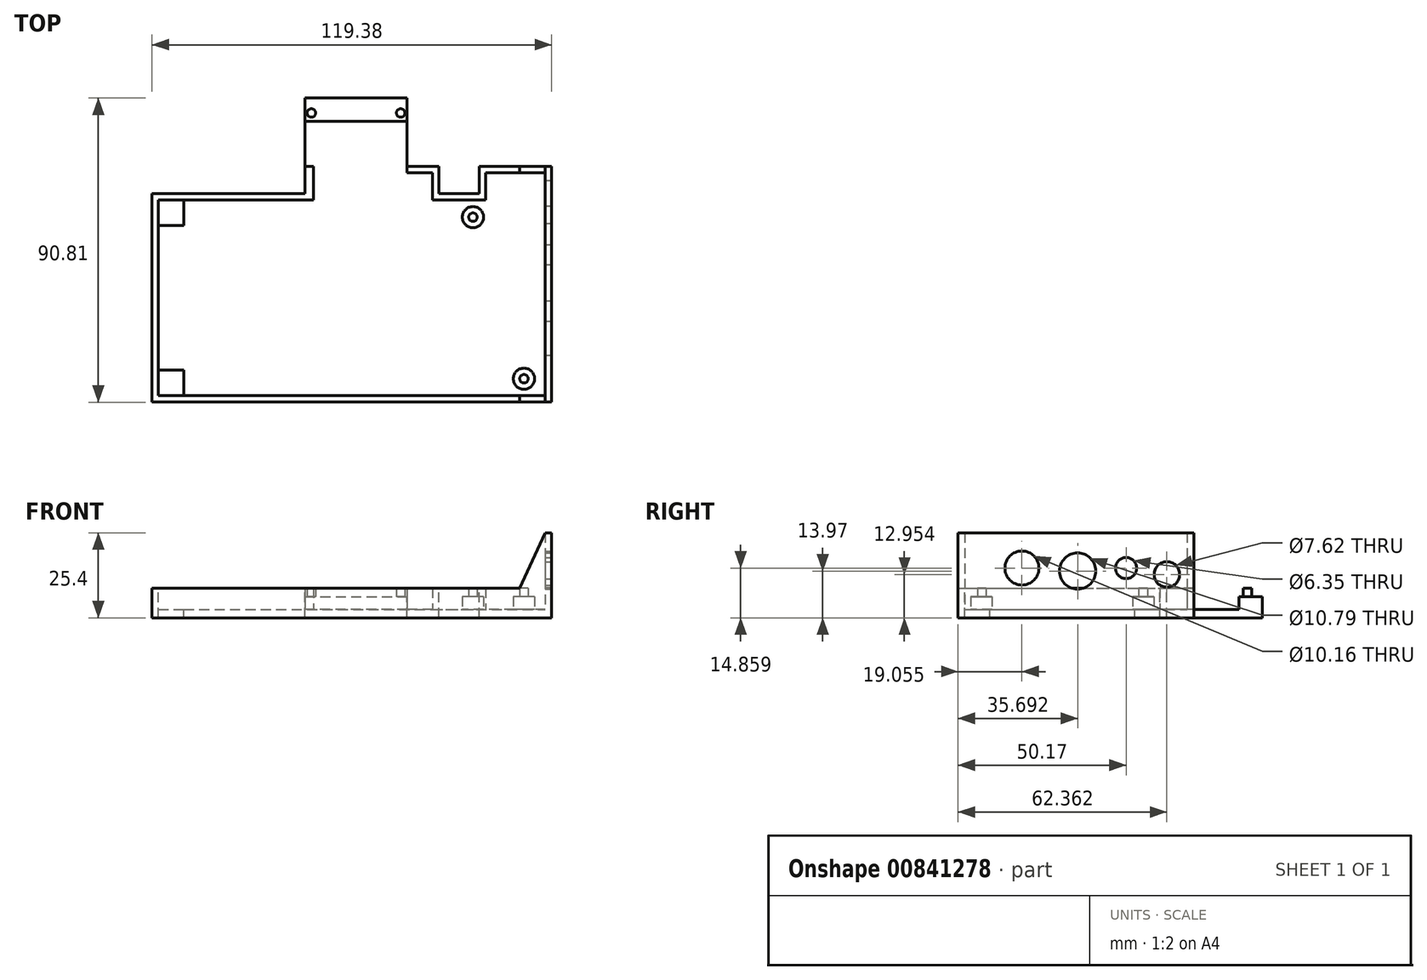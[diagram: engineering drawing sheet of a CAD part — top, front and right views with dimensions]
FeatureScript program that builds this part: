
annotation { "Feature Type Name" : "Feature", "Feature Type Description" : "" }
export const myFeature = defineFeature(function(context is Context, id is Id, definition is map)
    precondition{}
    {
        {
            var Q0;
            Q0=qCreatedBy(makeId("Top.planeOp"),FACE);
            var sketch = newSketch(context, id + "F0", { "sketchPlane" : qUnion([Q0])});
            skLineSegment(sketch, "E0.bottom", {"start": v(-113.03, 0) * mm, "end": v(0, 0) * mm, "construction": true});
            skLineSegment(sketch, "E0.top", {"start": v(-33.66, 55.88) * mm, "end": v(-15.24, 55.88) * mm, "construction": true});
            skLineSegment(sketch, "E0.left", {"start": v(0, 0) * mm, "end": v(0, 55.88) * mm, "construction": true});
            skLineSegment(sketch, "E0.right", {"start": v(-113.03, 0) * mm, "end": v(-113.03, 55.88) * mm, "construction": true});
            skCircle(sketch, "E1", {"center": v(-5.08, 3.81) * mm, "radius": 1.27 * mm});
            skCircle(sketch, "E2", {"center": v(-5.08, 3.81) * mm, "radius": 3.18 * mm});
            skLineSegment(sketch, "E3", {"start": v(0, 55.88) * mm, "end": v(0, 64) * mm, "construction": true});
            skLineSegment(sketch, "E4", {"start": v(0, 64) * mm, "end": v(-15.24, 64) * mm, "construction": true});
            skLineSegment(sketch, "E5", {"start": v(-15.24, 64) * mm, "end": v(-15.24, 55.88) * mm, "construction": true});
            skLineSegment(sketch, "E6", {"start": v(-33.65, 55.88) * mm, "end": v(-33.65, 64) * mm, "construction": true});
            skLineSegment(sketch, "E7", {"start": v(-33.66, 64) * mm, "end": v(-65.4, 64) * mm, "construction": true});
            skLineSegment(sketch, "E8", {"start": v(-65.4, 64) * mm, "end": v(-65.4, 55.88) * mm, "construction": true});
            skCircle(sketch, "E9", {"center": v(-20.32, 52.07) * mm, "radius": 3.18 * mm});
            skCircle(sketch, "E10", {"center": v(-20.32, 52.07) * mm, "radius": 1.27 * mm});
            skLineSegment(sketch, "E11.trimOffspring", {"start": v(-113.03, 55.88) * mm, "end": v(-65.4, 55.88) * mm, "construction": true});
            skLineSegment(sketch, "E12.0", {"start": v(-32.39, 57.15) * mm, "end": v(-16.51, 57.15) * mm});
            skLineSegment(sketch, "E12.1", {"start": v(-32.39, 57.15) * mm, "end": v(-32.39, 65.28) * mm});
            skLineSegment(sketch, "E12.4", {"start": v(-114.3, 57.15) * mm, "end": v(-67.95, 57.15) * mm});
            skLineSegment(sketch, "E12.5", {"start": v(-16.51, 65.28) * mm, "end": v(-16.51, 57.15) * mm});
            skLineSegment(sketch, "E12.6", {"start": v(1.27, 65.28) * mm, "end": v(-16.51, 65.28) * mm});
            skLineSegment(sketch, "E12.7", {"start": v(1.27, 65.28) * mm, "end": v(1.27, 65.28) * mm});
            skLineSegment(sketch, "E12.8", {"start": v(1.27, -1.27) * mm, "end": v(1.27, 65.28) * mm});
            skLineSegment(sketch, "E12.9", {"start": v(-114.3, -1.27) * mm, "end": v(1.27, -1.27) * mm});
            skLineSegment(sketch, "E12.10", {"start": v(-114.3, -1.27) * mm, "end": v(-114.3, 57.15) * mm});
            skLineSegment(sketch, "E13.bottom", {"start": v(-114.3, 57.15) * mm, "end": v(-106.68, 57.15) * mm});
            skLineSegment(sketch, "E13.top", {"start": v(-114.3, 49.53) * mm, "end": v(-106.68, 49.53) * mm});
            skLineSegment(sketch, "E13.left", {"start": v(-114.3, 57.15) * mm, "end": v(-114.3, 49.53) * mm});
            skLineSegment(sketch, "E13.right", {"start": v(-106.68, 57.15) * mm, "end": v(-106.68, 49.53) * mm});
            skLineSegment(sketch, "E14.bottom", {"start": v(-114.3, -1.27) * mm, "end": v(-106.68, -1.27) * mm});
            skLineSegment(sketch, "E14.top", {"start": v(-114.3, 6.35) * mm, "end": v(-106.68, 6.35) * mm});
            skLineSegment(sketch, "E14.left", {"start": v(-114.3, -1.27) * mm, "end": v(-114.3, 6.35) * mm});
            skLineSegment(sketch, "E14.right", {"start": v(-106.68, -1.27) * mm, "end": v(-106.68, 6.35) * mm});
            skLineSegment(sketch, "E15.0", {"start": v(-116.2, -3.17) * mm, "end": v(-116.2, 59.06) * mm});
            skLineSegment(sketch, "E15.1", {"start": v(-116.2, -3.17) * mm, "end": v(3.17, -3.17) * mm});
            skLineSegment(sketch, "E15.2", {"start": v(-116.2, 59.06) * mm, "end": v(-70.48, 59.06) * mm});
            skLineSegment(sketch, "E15.3", {"start": v(3.17, -3.17) * mm, "end": v(3.17, 67.18) * mm});
            skLineSegment(sketch, "E15.4", {"start": v(3.17, 67.18) * mm, "end": v(-18.41, 67.18) * mm});
            skLineSegment(sketch, "E15.5", {"start": v(-18.41, 67.18) * mm, "end": v(-18.41, 59.06) * mm});
            skLineSegment(sketch, "E15.7", {"start": v(-30.48, 67.18) * mm, "end": v(-40, 67.18) * mm});
            skLineSegment(sketch, "E15.8", {"start": v(-30.48, 59.06) * mm, "end": v(-30.48, 67.18) * mm});
            skLineSegment(sketch, "E15.9", {"start": v(-30.48, 59.06) * mm, "end": v(-18.41, 59.06) * mm});
            skLineSegment(sketch, "E16", {"start": v(-70.48, 59.06) * mm, "end": v(-70.48, 87.63) * mm});
            skLineSegment(sketch, "E17", {"start": v(-32.39, 65.28) * mm, "end": v(-43.18, 65.28) * mm});
            skCircle(sketch, "E18", {"center": v(-68.58, 83.19) * mm, "radius": 1.27 * mm});
            skLineSegment(sketch, "E19", {"start": v(-67.95, 80.65) * mm, "end": v(-43.18, 80.65) * mm});
            skLineSegment(sketch, "E20", {"start": v(-67.95, 80.65) * mm, "end": v(-67.95, 57.15) * mm});
            skLineSegment(sketch, "E21", {"start": v(-43.18, 80.65) * mm, "end": v(-43.18, 65.28) * mm});
            skCircle(sketch, "E22", {"center": v(-41.91, 83.19) * mm, "radius": 1.27 * mm});
            skLineSegment(sketch, "E23", {"start": v(-70.48, 87.63) * mm, "end": v(-40, 87.63) * mm});
            skLineSegment(sketch, "E24", {"start": v(-40, 87.63) * mm, "end": v(-40, 67.18) * mm});
            skLineSegment(sketch, "E25", {"start": v(-67.95, 80.65) * mm, "end": v(-70.48, 80.65) * mm});
            skLineSegment(sketch, "E26", {"start": v(-43.18, 80.65) * mm, "end": v(-40, 80.65) * mm});
            skLineSegment(sketch, "E27", {"start": v(1.27, -1.27) * mm, "end": v(1.27, -3.17) * mm});
            skLineSegment(sketch, "E28", {"start": v(1.27, 65.28) * mm, "end": v(1.27, 67.18) * mm});
            skLineSegment(sketch, "E29", {"start": v(-67.95, 67.18) * mm, "end": v(-70.48, 67.18) * mm});
            skLineSegment(sketch, "E30", {"start": v(-40, 67.18) * mm, "end": v(-40, 65.28) * mm});
            skSolve(sketch);
        }
        {
            var Q0;
            Q0=makeQuery(id+"F0.imprint","IMPRINT",FACE,{"disambiguationData":[TD([[makeQuery(id+"F0.imprint","IMPRINT",EDGE,{"derivedFrom":sQuery(id+"F0.wireOp",EDGE,"E12.0")}),1.0]])]});
            var Q1;
            Q1=makeQuery(id+"F0.imprint","IMPRINT",FACE,{"disambiguationData":[TD([[makeQuery(id+"F0.imprint","IMPRINT",EDGE,{"derivedFrom":sQuery(id+"F0.wireOp",EDGE,"E2")}),-1.0]])]});
            var Q2;
            Q2=makeQuery(id+"F0.imprint","IMPRINT",FACE,{"disambiguationData":[TD([[makeQuery(id+"F0.imprint","IMPRINT",EDGE,{"derivedFrom":sQuery(id+"F0.wireOp",EDGE,"E13.bottom")}),-1.0]])]});
            var Q3;
            Q3=makeQuery(id+"F0.imprint","IMPRINT",FACE,{"disambiguationData":[TD([[makeQuery(id+"F0.imprint","IMPRINT",EDGE,{"derivedFrom":sQuery(id+"F0.wireOp",EDGE,"E14.bottom")}),1.0]])]});
            var Q4;
            Q4=makeQuery(id+"F0.imprint","IMPRINT",FACE,{"disambiguationData":[TD([[makeQuery(id+"F0.imprint","IMPRINT",EDGE,{"derivedFrom":sQuery(id+"F0.wireOp",EDGE,"E18")}),-1.0]])]});
            var Q5;
            Q5=makeQuery(id+"F0.imprint","IMPRINT",FACE,{"disambiguationData":[TD([[makeQuery(id+"F0.imprint","IMPRINT",EDGE,{"derivedFrom":sQuery(id+"F0.wireOp",EDGE,"E18")}),1.0]])]});
            var Q6;
            Q6=makeQuery(id+"F0.imprint","IMPRINT",FACE,{"disambiguationData":[TD([[makeQuery(id+"F0.imprint","IMPRINT",EDGE,{"derivedFrom":sQuery(id+"F0.wireOp",EDGE,"E22")}),1.0]])]});
            var Q7;
            Q7=makeQuery(id+"F0.imprint","IMPRINT",FACE,{"disambiguationData":[TD([[makeQuery(id+"F0.imprint","IMPRINT",EDGE,{"derivedFrom":sQuery(id+"F0.wireOp",EDGE,"E9")}),1.0]])]});
            var Q8;
            Q8=makeQuery(id+"F0.imprint","IMPRINT",FACE,{"disambiguationData":[TD([[makeQuery(id+"F0.imprint","IMPRINT",EDGE,{"derivedFrom":sQuery(id+"F0.wireOp",EDGE,"E10")}),1.0]])]});
            var Q9;
            Q9=makeQuery(id+"F0.imprint","IMPRINT",FACE,{"disambiguationData":[TD([[makeQuery(id+"F0.imprint","IMPRINT",EDGE,{"derivedFrom":sQuery(id+"F0.wireOp",EDGE,"E1")}),-1.0]])]});
            var Q10;
            Q10=makeQuery(id+"F0.imprint","IMPRINT",FACE,{"disambiguationData":[TD([[makeQuery(id+"F0.imprint","IMPRINT",EDGE,{"derivedFrom":sQuery(id+"F0.wireOp",EDGE,"E1")}),1.0]])]});
            var Q11;
            Q11=makeQuery(id+"F0.imprint","IMPRINT",FACE,{"disambiguationData":[TD([[makeQuery(id+"F0.imprint","IMPRINT",EDGE,{"derivedFrom":sQuery(id+"F0.wireOp",EDGE,"E12.4")}),1.0]])]});
            var Q12;
            Q12=makeQuery(id+"F0.imprint","IMPRINT",FACE,{"disambiguationData":[TD([[makeQuery(id+"F0.imprint","IMPRINT",EDGE,{"derivedFrom":sQuery(id+"F0.wireOp",EDGE,"E12.8")}),-1.0]])]});
            var Q13;
            {var subQ0=sQuery(id+"F0.wireOp",EDGE,"E25");Q13=makeQuery(id+"F0.imprint","IMPRINT",FACE,{"disambiguationData":[TD([[makeQuery(id+"F0.imprint","IMPRINT",EDGE,{"derivedFrom":subQ0}),1.0]])]});}
            var Q14;
            {var subQ0=sQuery(id+"F0.wireOp",EDGE,"E26");Q14=makeQuery(id+"F0.imprint","IMPRINT",FACE,{"disambiguationData":[TD([[makeQuery(id+"F0.imprint","IMPRINT",EDGE,{"derivedFrom":subQ0}),-1.0]])]});}
            extrude(context, id + "F1", {"entities" : qUnion([Q0, Q1, Q2, Q3, Q4, Q5, Q6, Q7, Q8, Q9, Q10, Q11, Q12, Q13, Q14]), "oppositeDirection" : true, "depth" : 2.54 * mm, "offsetDistance" : 25.4 * mm});
        }
        {
            var Q0;
            Q0=makeQuery(id+"F0.imprint","IMPRINT",FACE,{"disambiguationData":[TD([[makeQuery(id+"F0.imprint","IMPRINT",EDGE,{"derivedFrom":sQuery(id+"F0.wireOp",EDGE,"E18")}),-1.0]])]});
            var Q1;
            Q1=makeQuery(id+"F0.imprint","IMPRINT",FACE,{"disambiguationData":[TD([[makeQuery(id+"F0.imprint","IMPRINT",EDGE,{"derivedFrom":sQuery(id+"F0.wireOp",EDGE,"E18")}),1.0]])]});
            var Q2;
            Q2=makeQuery(id+"F0.imprint","IMPRINT",FACE,{"disambiguationData":[TD([[makeQuery(id+"F0.imprint","IMPRINT",EDGE,{"derivedFrom":sQuery(id+"F0.wireOp",EDGE,"E22")}),1.0]])]});
            var Q3;
            Q3=makeQuery(id+"F0.imprint","IMPRINT",FACE,{"disambiguationData":[TD([[makeQuery(id+"F0.imprint","IMPRINT",EDGE,{"derivedFrom":sQuery(id+"F0.wireOp",EDGE,"E13.bottom")}),-1.0]])]});
            var Q4;
            Q4=makeQuery(id+"F0.imprint","IMPRINT",FACE,{"disambiguationData":[TD([[makeQuery(id+"F0.imprint","IMPRINT",EDGE,{"derivedFrom":sQuery(id+"F0.wireOp",EDGE,"E14.bottom")}),1.0]])]});
            var Q5;
            Q5=makeQuery(id+"F0.imprint","IMPRINT",FACE,{"disambiguationData":[TD([[makeQuery(id+"F0.imprint","IMPRINT",EDGE,{"derivedFrom":sQuery(id+"F0.wireOp",EDGE,"E9")}),1.0]])]});
            var Q6;
            Q6=makeQuery(id+"F0.imprint","IMPRINT",FACE,{"disambiguationData":[TD([[makeQuery(id+"F0.imprint","IMPRINT",EDGE,{"derivedFrom":sQuery(id+"F0.wireOp",EDGE,"E10")}),1.0]])]});
            var Q7;
            Q7=makeQuery(id+"F0.imprint","IMPRINT",FACE,{"disambiguationData":[TD([[makeQuery(id+"F0.imprint","IMPRINT",EDGE,{"derivedFrom":sQuery(id+"F0.wireOp",EDGE,"E1")}),1.0]])]});
            var Q8;
            Q8=makeQuery(id+"F0.imprint","IMPRINT",FACE,{"disambiguationData":[TD([[makeQuery(id+"F0.imprint","IMPRINT",EDGE,{"derivedFrom":sQuery(id+"F0.wireOp",EDGE,"E1")}),-1.0]])]});
            extrude(context, id + "F2", {"entities" : qUnion([Q0, Q1, Q2, Q3, Q4, Q5, Q6, Q7, Q8]), "operationType" : NewBodyOperationType.ADD, "depth" : 3.8 * mm, "offsetDistance" : 25.4 * mm});
        }
        {
            var Q0;
            Q0=makeQuery(id+"F0.imprint","IMPRINT",FACE,{"disambiguationData":[TD([[makeQuery(id+"F0.imprint","IMPRINT",EDGE,{"derivedFrom":sQuery(id+"F0.wireOp",EDGE,"E18")}),1.0]])]});
            var Q1;
            Q1=makeQuery(id+"F0.imprint","IMPRINT",FACE,{"disambiguationData":[TD([[makeQuery(id+"F0.imprint","IMPRINT",EDGE,{"derivedFrom":sQuery(id+"F0.wireOp",EDGE,"E22")}),1.0]])]});
            var Q2;
            Q2=makeQuery(id+"F0.imprint","IMPRINT",FACE,{"disambiguationData":[TD([[makeQuery(id+"F0.imprint","IMPRINT",EDGE,{"derivedFrom":sQuery(id+"F0.wireOp",EDGE,"E10")}),1.0]])]});
            var Q3;
            Q3=makeQuery(id+"F0.imprint","IMPRINT",FACE,{"disambiguationData":[TD([[makeQuery(id+"F0.imprint","IMPRINT",EDGE,{"derivedFrom":sQuery(id+"F0.wireOp",EDGE,"E1")}),1.0]])]});
            var Q4;
            {var subQ1=sQuery(id+"F0.wireOp",EDGE,"E12.4");Q4=makeQuery(id+"F0.imprint","IMPRINT",FACE,{"disambiguationData":[TD([[makeQuery(id+"F0.imprint","IMPRINT",EDGE,{"derivedFrom":subQ1}),1.0]])]});}
            var Q5;
            Q5=makeQuery(id+"F0.imprint","IMPRINT",FACE,{"disambiguationData":[TD([[makeQuery(id+"F0.imprint","IMPRINT",EDGE,{"derivedFrom":sQuery(id+"F0.wireOp",EDGE,"E12.0")}),1.0]])]});
            extrude(context, id + "F3", {"entities" : qUnion([Q0, Q1, Q2, Q3, Q4, Q5]), "operationType" : NewBodyOperationType.ADD, "depth" : 6.35 * mm, "offsetDistance" : 25.4 * mm});
        }
        {
            var Q0;
            Q0=makeQuery(id+"F0.imprint","IMPRINT",FACE,{"disambiguationData":[TD([[makeQuery(id+"F0.imprint","IMPRINT",EDGE,{"derivedFrom":sQuery(id+"F0.wireOp",EDGE,"E12.8")}),-1.0]])]});
            extrude(context, id + "F4", {"entities" : qUnion([Q0]), "operationType" : NewBodyOperationType.ADD, "depth" : 22.86 * mm, "offsetDistance" : 25.4 * mm});
        }
        {
            var Q0;
            {var subQ0=sQuery(id+"F0.wireOp",EDGE,"E15.3");Q0=makeQuery(id+"F4.boolean.opBoolean","MERGE",FACE,{"derivedFrom":[makeQuery(id+"F1.opExtrude","SWEPT_FACE",FACE,{"disambiguationData":[OSD([subQ0])]}),makeQuery(id+"F4.opExtrude","SWEPT_FACE",FACE,{"disambiguationData":[OSD([subQ0])]})]});}
            var sketch = newSketch(context, id + "F5", { "sketchPlane" : qUnion([Q0])});
            skCircle(sketch, "E31", {"center": v(15.88, 12.32) * mm, "radius": 5.08 * mm});
            skCircle(sketch, "E32", {"center": v(32.51, 11.43) * mm, "radius": 5.4 * mm});
            skCircle(sketch, "E33", {"center": v(47, 12.32) * mm, "radius": 3.18 * mm});
            skCircle(sketch, "E34", {"center": v(59.18, 10.41) * mm, "radius": 3.81 * mm});
            skLineSegment(sketch, "E35", {"start": v(80.65, 3.81) * mm, "end": v(-3.17, 3.8) * mm, "construction": true});
            skSolve(sketch);
        }
        {
            var Q0;
            Q0 = qSketchRegion(id + "F5", true);
            var Q1;
            Q1=makeQuery(id+"F4.opExtrude","SWEPT_FACE",FACE,{"disambiguationData":[OSD([sQuery(id+"F0.wireOp",EDGE,"E12.8"),sQuery(id+"F0.wireOp",EDGE,"E27"),sQuery(id+"F0.wireOp",EDGE,"E28")])]});
            extrude(context, id + "F6", {"entities" : qUnion([Q0]), "operationType" : NewBodyOperationType.REMOVE, "endBound" : BoundingType.UP_TO_NEXT, "oppositeDirection" : true, "depth" : 2.54 * mm, "endBoundEntityFace" : qUnion([Q1]), "offsetDistance" : 25.4 * mm});
        }
        {
            var Q0;
            {var subQ0=sQuery(id+"F0.wireOp",EDGE,"E15.4");Q0=makeQuery(id+"F4.boolean.opBoolean","MERGE",FACE,{"derivedFrom":[makeQuery(id+"F3.boolean.opBoolean","MERGE",FACE,{"derivedFrom":[makeQuery(id+"F1.opExtrude","SWEPT_FACE",FACE,{"disambiguationData":[OSD([subQ0])]}),makeQuery(id+"F3.opExtrude","SWEPT_FACE",FACE,{"disambiguationData":[OSD([subQ0])]})]}),makeQuery(id+"F4.opExtrude","SWEPT_FACE",FACE,{"disambiguationData":[OSD([subQ0])]})]});}
            var sketch = newSketch(context, id + "F7", { "sketchPlane" : qUnion([Q0])});
            skLineSegment(sketch, "E36", {"start": v(-1.27, 22.86) * mm, "end": v(6.43, 6.35) * mm});
            skLineSegment(sketch, "E37", {"start": v(6.43, 6.35) * mm, "end": v(-1.27, 6.35) * mm});
            skLineSegment(sketch, "E38", {"start": v(-1.27, 6.35) * mm, "end": v(-1.27, 22.86) * mm});
            skSolve(sketch);
        }
        {
            var Q0;
            Q0 = qSketchRegion(id + "F7", true);
            var Q1;
            Q1=makeQuery(id+"F3.opExtrude","SWEPT_FACE",FACE,{"disambiguationData":[OSD([sQuery(id+"F0.wireOp",EDGE,"E12.6")])]});
            var Q2;
            Q2=makeQuery(id+"F3.opExtrude","SWEPT_FACE",FACE,{"disambiguationData":[OSD([sQuery(id+"F0.wireOp",EDGE,"E12.6")])]});
            extrude(context, id + "F8", {"entities" : qUnion([Q0]), "operationType" : NewBodyOperationType.ADD, "endBound" : BoundingType.UP_TO_SURFACE, "oppositeDirection" : true, "depth" : 25.4 * mm, "endBoundEntityFace" : qUnion([Q1]), "offsetDistance" : 25.4 * mm});
        }
        {
            var Q0;
            Q0 = qSketchRegion(id + "F7", true);
            var Q1;
            {var subQ0=sQuery(id+"F0.wireOp",EDGE,"E15.1");Q1=makeQuery(id+"F4.boolean.opBoolean","MERGE",FACE,{"derivedFrom":[makeQuery(id+"F3.boolean.opBoolean","MERGE",FACE,{"derivedFrom":[makeQuery(id+"F1.opExtrude","SWEPT_FACE",FACE,{"disambiguationData":[OSD([subQ0])]}),makeQuery(id+"F3.opExtrude","SWEPT_FACE",FACE,{"disambiguationData":[OSD([subQ0])]})]}),makeQuery(id+"F4.opExtrude","SWEPT_FACE",FACE,{"disambiguationData":[OSD([subQ0])]})]});}
            var Q2;
            Q2=makeQuery(id+"F3.opExtrude","SWEPT_FACE",FACE,{"disambiguationData":[OSD([sQuery(id+"F0.wireOp",EDGE,"E12.9"),sQuery(id+"F0.wireOp",EDGE,"E14.bottom")])]});
            extrude(context, id + "F9", {"entities" : qUnion([Q0]), "operationType" : NewBodyOperationType.ADD, "endBound" : BoundingType.UP_TO_SURFACE, "oppositeDirection" : true, "depth" : 76.56 * mm, "endBoundEntityFace" : qUnion([Q1]), "offsetDistance" : 25.4 * mm, "hasSecondDirection" : true, "secondDirectionBound" : SecondDirectionBoundingType.UP_TO_SURFACE, "secondDirectionOppositeDirection" : true, "secondDirectionDepth" : 25.4 * mm, "secondDirectionBoundEntityFace" : qUnion([Q2])});
        }
    });
